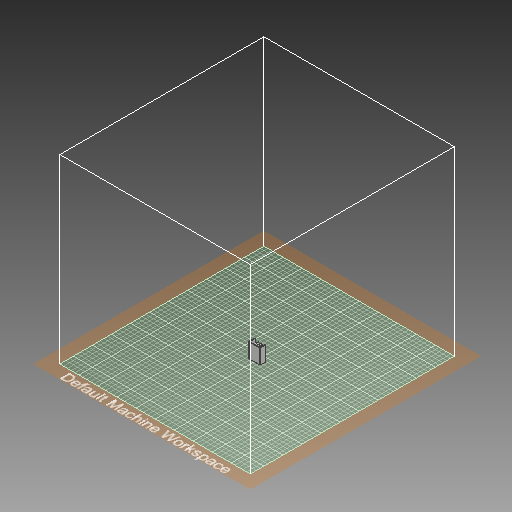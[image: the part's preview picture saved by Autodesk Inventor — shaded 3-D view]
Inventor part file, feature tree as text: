
AUTODESK INVENTOR PART (.ipt)
format: ipt  version: 2019.3 (Build 233278000, 278)  size: 1,136,128 bytes
history: native  units: mm
features: extrude x4, sketch x4, mirror x1, other x1, plane x1, projected_geometry x1
ambient origin geometry x8: Origin, YZ Plane, XZ Plane, XY Plane, X Axis, Y Axis, Z Axis, Center Point
bodies: Body1 (feature_tree)
feature tree (12):
  extrude  "Extrusion2"  Depth=0.5mm
  extrude  "Extrusion4"  Depth=0.5mm
  mirror  "Mirror1"
  extrude  "Extrusion5"  Depth=0.5mm
  extrude  "Extrusion6"  Depth=1.0mm TaperAngle=360.0deg
  sketch  "Sketch5"  dims[d9=30.0deg d10=400.0mm d12=360.0deg d14=10.0mm d15=0.0mm d16=0.15mm d17=15.0mm d20=22.68928mm d21=2.0mm d22=2.0mm d23=10.0mm d24=10.0mm d25=2.0mm d26=4.0mm d27=2.0mm d28=1.0mm d29=1.0mm d30=1.0mm d31=1.0mm d32=11.0mm d34=10.0mm d35=0.0mm d36=3.0mm d37=0.0mm d38=1.0mm d39=0.0mm]
  other  "Work Axis1"
  plane  "Work Plane1"
  sketch  "Sketch2"  dims[d3=5.047545mm d4=0.5mm]
  projected_geometry  "Projected Loop1"
  sketch  "Sketch3"  dims[d5=0.5mm d6=0.5mm]
  sketch  "Sketch4"  dims[d7=60.0deg d8=0.5mm]
